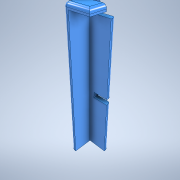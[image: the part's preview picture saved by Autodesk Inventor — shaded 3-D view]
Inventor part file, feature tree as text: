
AUTODESK INVENTOR PART (.ipt)
format: ipt  version: 2021 (Build 250183000, 183)  size: 166,912 bytes
history: native  units: mm
features: extrude x5, sketch x4, fillet x1
ambient origin geometry x8: Origin, YZ Plane, XZ Plane, XY Plane, X Axis, Y Axis, Z Axis, Center Point
bodies: Solid1 (feature_tree)
feature tree (10):
  extrude  "Extrusion1"  Depth=15.0mm
  extrude  "Extrusion3"  Depth=3.0mm
  extrude  "Extrusion4"  Depth=12.0mm
  fillet  "Fillet3"  Radius=3.0mm
  extrude  "Extrusion7"  Depth=12.0mm TaperAngle=0.0deg
  extrude  "Extrusion8"  Depth=2.0mm
  sketch  "Sketch4"  dims[d0=15.0mm d1=15.0mm]
  sketch  "Sketch6"  dims[d2=86.0mm d3=0.0mm d10=3.0mm]
  sketch  "Sketch11"  dims[d11=12.0mm d12=12.0mm d13=3.0mm]
  sketch  "Sketch12"  dims[d14=3.0mm d15=0.0mm d16=12.0mm d17=0.0mm d18=2.0mm d31=6.5mm d32=0.0mm d39=0.0mm d40=0.0mm d44=3.5mm d45=9.0mm]
